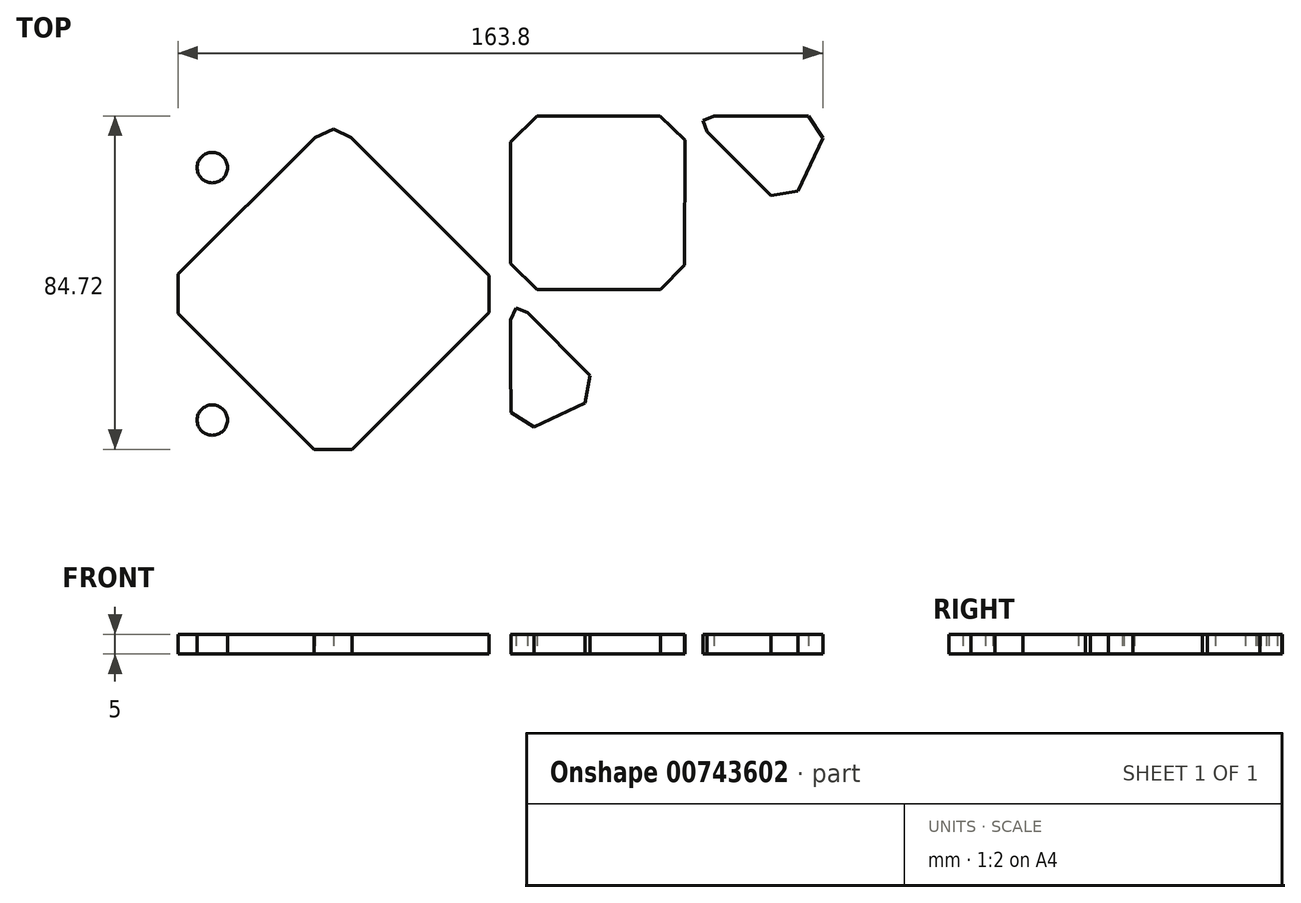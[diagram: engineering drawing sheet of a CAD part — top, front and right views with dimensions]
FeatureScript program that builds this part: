
annotation { "Feature Type Name" : "Feature", "Feature Type Description" : "" }
export const myFeature = defineFeature(function(context is Context, id is Id, definition is map)
    precondition{}
    {
        {
            var Q0;
            Q0=qCreatedBy(makeId("Top.planeOp"),FACE);
            var sketch = newSketch(context, id + "F0", { "sketchPlane" : qUnion([Q0])});
            skLineSegment(sketch, "E0", {"start": v(-42.4, 38.98) * mm, "end": v(-37.94, 36.89) * mm});
            skLineSegment(sketch, "E1", {"start": v(-37.94, 36.89) * mm, "end": v(-23.74, 22.67) * mm});
            skLineSegment(sketch, "E2", {"start": v(-23.74, 22.67) * mm, "end": v(-2.86, 1.78) * mm});
            skLineSegment(sketch, "E3", {"start": v(-2.86, 1.78) * mm, "end": v(-2.9, -7.57) * mm});
            skLineSegment(sketch, "E4", {"start": v(-2.9, -7.57) * mm, "end": v(-37.68, -42.36) * mm});
            skLineSegment(sketch, "E5", {"start": v(-37.68, -42.36) * mm, "end": v(-47.3, -42.36) * mm});
            skLineSegment(sketch, "E6", {"start": v(-47.3, -42.36) * mm, "end": v(-81.88, -7.87) * mm});
            skLineSegment(sketch, "E7", {"start": v(-81.88, -7.87) * mm, "end": v(-81.9, 2.14) * mm});
            skLineSegment(sketch, "E8", {"start": v(-81.9, 2.14) * mm, "end": v(-47.1, 36.9) * mm});
            skLineSegment(sketch, "E9", {"start": v(-47.1, 36.9) * mm, "end": v(-42.4, 38.98) * mm});
            skLineSegment(sketch, "E10", {"start": v(24.6, -1.76) * mm, "end": v(9.27, -1.76) * mm});
            skLineSegment(sketch, "E11", {"start": v(9.27, -1.76) * mm, "end": v(2.64, 4.87) * mm});
            skLineSegment(sketch, "E12", {"start": v(2.64, 4.87) * mm, "end": v(2.64, 35.72) * mm});
            skLineSegment(sketch, "E13", {"start": v(2.64, 35.72) * mm, "end": v(9.3, 42.31) * mm});
            skLineSegment(sketch, "E14", {"start": v(9.3, 42.31) * mm, "end": v(40.5, 42.36) * mm});
            skLineSegment(sketch, "E15", {"start": v(40.5, 42.36) * mm, "end": v(46.84, 36.16) * mm});
            skLineSegment(sketch, "E16", {"start": v(46.84, 36.16) * mm, "end": v(46.78, 4.43) * mm});
            skLineSegment(sketch, "E17", {"start": v(46.78, 4.43) * mm, "end": v(40.65, -1.75) * mm});
            skLineSegment(sketch, "E18", {"start": v(40.65, -1.75) * mm, "end": v(24.6, -1.76) * mm});
            skLineSegment(sketch, "E19", {"start": v(2.63, -21.23) * mm, "end": v(2.63, -10.67) * mm});
            skLineSegment(sketch, "E20", {"start": v(2.63, -10.67) * mm, "end": v(2.64, -9.44) * mm});
            skLineSegment(sketch, "E21", {"start": v(2.64, -9.44) * mm, "end": v(3.97, -6.4) * mm});
            skLineSegment(sketch, "E22", {"start": v(3.97, -6.4) * mm, "end": v(6.89, -7.63) * mm});
            skLineSegment(sketch, "E23", {"start": v(6.89, -7.63) * mm, "end": v(22.81, -23.57) * mm});
            skLineSegment(sketch, "E24", {"start": v(22.81, -23.57) * mm, "end": v(21.54, -30.6) * mm});
            skLineSegment(sketch, "E25", {"start": v(21.54, -30.6) * mm, "end": v(8.5, -36.74) * mm});
            skLineSegment(sketch, "E26", {"start": v(8.5, -36.74) * mm, "end": v(2.65, -33.03) * mm});
            skLineSegment(sketch, "E27", {"start": v(2.65, -33.03) * mm, "end": v(2.63, -21.23) * mm});
            skLineSegment(sketch, "E28", {"start": v(66.6, 42.3) * mm, "end": v(78.23, 42.3) * mm});
            skLineSegment(sketch, "E29", {"start": v(78.23, 42.3) * mm, "end": v(81.9, 36.67) * mm});
            skLineSegment(sketch, "E30", {"start": v(81.9, 36.67) * mm, "end": v(75.56, 23.31) * mm});
            skLineSegment(sketch, "E31", {"start": v(75.56, 23.31) * mm, "end": v(68.75, 22.15) * mm});
            skLineSegment(sketch, "E32", {"start": v(68.75, 22.15) * mm, "end": v(52.53, 38.36) * mm});
            skLineSegment(sketch, "E33", {"start": v(52.53, 38.36) * mm, "end": v(51.5, 41.13) * mm});
            skLineSegment(sketch, "E34", {"start": v(51.5, 41.13) * mm, "end": v(54.24, 42.3) * mm});
            skLineSegment(sketch, "E35", {"start": v(54.24, 42.3) * mm, "end": v(66.6, 42.3) * mm});
            skLineSegment(sketch, "E36", {"start": v(-42.4, 38.98) * mm, "end": v(-81.9, 38.9) * mm, "construction": true});
            skPoint(sketch, "E36.endSnap0", {"position": v(-81.9, -2.86) * mm});
            skLineSegment(sketch, "E37", {"start": v(-81.9, 38.9) * mm, "end": v(-81.9, -2.86) * mm, "construction": true});
            skLineSegment(sketch, "E38", {"start": v(-64.5, 19.52) * mm, "end": v(-81.9, 38.9) * mm, "construction": true});
            skCircle(sketch, "E39", {"center": v(-73.2, 29.2) * mm, "radius": 3.86 * mm});
            skLineSegment(sketch, "E40", {"start": v(-81.9, -2.86) * mm, "end": v(-2.88, -2.86) * mm, "construction": true});
            skCircle(sketch, "E41.MirrorC", {"center": v(-73.2, -34.93) * mm, "radius": 3.86 * mm});
            skSolve(sketch);
        }
        {
            var Q0;
            Q0 = qSketchRegion(id + "F0", true);
            extrude(context, id + "F1", {"entities" : qUnion([Q0]), "depth" : 5 * mm, "offsetDistance" : 25 * mm});
        }
    });
